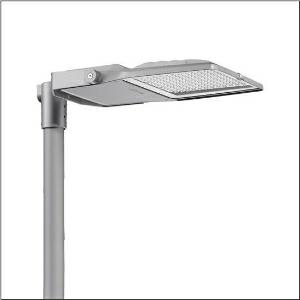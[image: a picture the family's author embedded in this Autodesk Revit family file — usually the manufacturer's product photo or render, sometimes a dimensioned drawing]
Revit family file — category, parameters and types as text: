
# Revit family: floodlight_fl_21_iq_midi___pl33t_5xa7782e2f3a_552b
name_source: partatom
category: Lighting Fixtures
units: mm (PartAtom-declared; Revit-internal decimal feet)

## family parameters
Cut with Voids When Loaded = No
Host = Face
Light Source = No
Part Type = Normal
Room Calculation Point = No
Round Connector Dimension = Use Diameter
Shared = No

## types (1)
- --- (1 x LED, 26540 lm, 208.1 W, 3000K)
    Apparent Load = 208 VA
    CIE Flux Codes = 26 75 99 100 100
    Color Rendering = 70
    Color Temperature = 3000K
    Default Elevation = 1800 mm
    Description = Floodlight FL 21 iQ midi, floodlight, primary light control with lens, of PMMA, primary optical cover: protective disc, of toughened safety glass, transparent, light distribution: PL33T, light emission: direct distribution, installation type: surface-mounted, lamps: LED, High Power LED, rated values: 26.540lm | 208,1W | 127,5lm/W (begin service life); end service life: 26.540lm | 227,1W; at 50% lumin. flux: 13.270lm | 90,1W | 147,3lm/W, colour temperature: 3000K, colour rendering: CRI > 70, light colour: 730, light setting 1 begin service life: 100% | 26.540lm | 208,1W | 127,5lm/W | 3.000K, light setting 1 end service life: 227,1W, further light settings possible, control: optimised constant luminous flux control (CLO 2.0), Desk-Remote (wireless, voltage-free reading and setting of iQ features in the workshop via application-optimized NFC function/RFID function), Smart-Wire, Night-Set, Temp-Guard, Auto-Match, Street-Remote, pre-setting: linear dimming characteristic, with terminal, 6-pole, mains connection: 220..240V, AC, 50/60Hz, luminaire housing, of diecast aluminium, powder-coated, SITECO metallic grey (DB 702S), corrosivity category C5 mid according to DIN EN ISO 12944suitable for swimming poolschlorine-resistant, sealing non-destructively replaceable, please order mast flange separately, mast bracket, of steel, galvanised, powder-coated, SITECO metallic grey (DB 702S), protection rating (complete): IP66, insulation class (complete): insulation class II (safety insulation), certification: CE, ENEC, VDE, protection symbol: D, impact resistance: IK08, permissible operating ambient temperature: -40..+40°C, permissible operating ambient temperature for outdoor applications: -40..+50°C, standard: DIN EN 12944, LABS conformity tested according to VDMA 24364:2018-05, packaging unit: 1 piece

Light Distribution: PL33T
    Height = 76 mm
    Lamp = 1 x LED
    Lamp Light Flux = 26540 lm
    Lamp Power = 208.1 W
    Lamp count = 1
    Length = 657 mm
    Luminous efficacy = 128 lm/W
    Manufacturer = Siteco
    ModVariant = No
    Model = 5XA7782E2F3A
    Number of Poles = 1
    OnlyDefault = Yes
    Power Factor = 1
    Product Name = Floodlight FL 21 iQ midi | PL33T
    Product group = floodlight | pylon annexe
    ProductGroupID = 6201
    Protection Class = Protection class II
    Protection Degree = IP 66
    RLX_Detail_Level = 1
    RLX_Emergency_Light_Flux = 0 lm
    RLX_Emergency_Type = 0
    RLX_Emergency_Type_DB = No
    RlxData = <blob elided: 154125 chars, md5=b45cc9b9>
    Socket = socket
    Standby Power = 0 W
    System Light Flux = 26540 lm
    System Power = 208 W
    Type Comments = factory setting: luminous flux: 100 % | dim-lin: 254 | 710 mA
    Type Image = l_1007123.jpg
    URL = http://relux.com
    VarID = @adj_103775
    Voltage = 0 V
    Weight = 0.00 kg
    Width = 442 mm

## geometry (parser evidence)
native form markers: Blend x4, Sweep x13
no freeform markers — native parametric forms only
